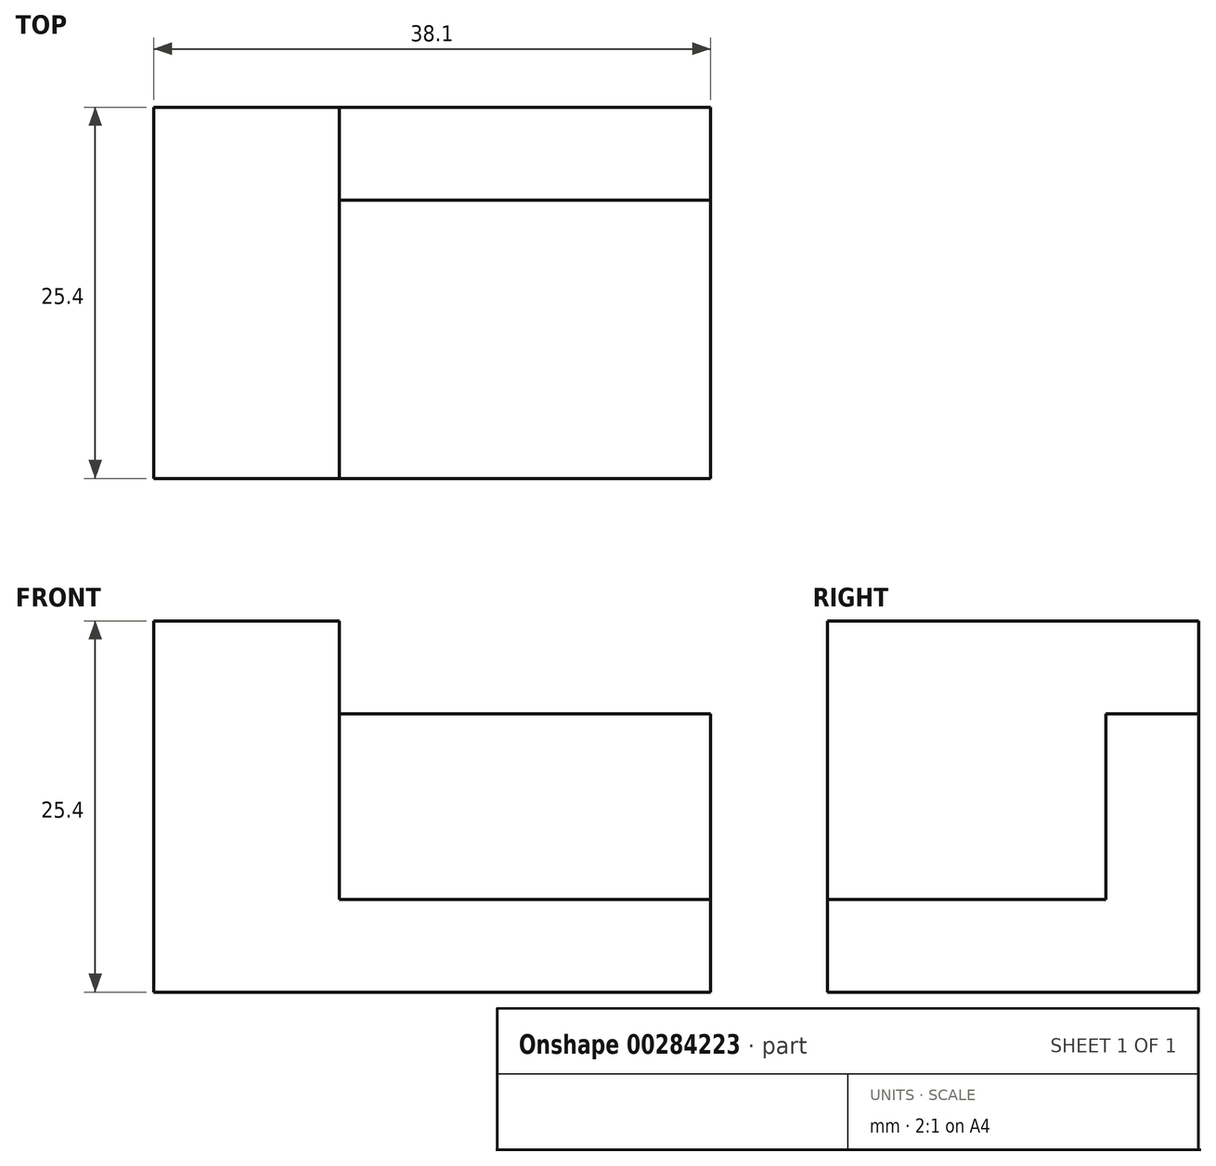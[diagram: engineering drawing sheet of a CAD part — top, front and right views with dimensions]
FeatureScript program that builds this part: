
annotation { "Feature Type Name" : "Feature", "Feature Type Description" : "" }
export const myFeature = defineFeature(function(context is Context, id is Id, definition is map)
    precondition{}
    {
        {
            var Q0;
            Q0=qCreatedBy(makeId("Front.planeOp"),FACE);
            var sketch = newSketch(context, id + "F0", { "sketchPlane" : qUnion([Q0])});
            skLineSegment(sketch, "E0", {"start": v(0, 25.4) * mm, "end": v(0, 0) * mm});
            skLineSegment(sketch, "E1", {"start": v(0, 0) * mm, "end": v(38.1, 0) * mm});
            skLineSegment(sketch, "E2", {"start": v(38.1, 0) * mm, "end": v(38.1, 6.35) * mm});
            skLineSegment(sketch, "E3", {"start": v(38.1, 6.35) * mm, "end": v(12.7, 6.35) * mm});
            skLineSegment(sketch, "E4", {"start": v(12.7, 6.35) * mm, "end": v(12.7, 25.4) * mm});
            skLineSegment(sketch, "E5", {"start": v(12.7, 25.4) * mm, "end": v(0, 25.4) * mm});
            skLineSegment(sketch, "E6", {"start": v(12.7, 19.05) * mm, "end": v(38.1, 19.05) * mm});
            skLineSegment(sketch, "E7", {"start": v(38.1, 19.05) * mm, "end": v(38.1, 6.35) * mm});
            skSolve(sketch);
        }
        {
            var Q0;
            Q0 = qSketchRegion(id + "F0", true);
            extrude(context, id + "F1", {"entities" : qUnion([Q0]), "depth" : 25.4 * mm});
        }
        {
            var Q0;
            Q0=makeQuery(id+"F1.opExtrude","SWEPT_FACE",FACE,{"disambiguationData":[OSD([sQuery(id+"F0.wireOp",EDGE,"E2"),sQuery(id+"F0.wireOp",EDGE,"E7")])]});
            var sketch = newSketch(context, id + "F2", { "sketchPlane" : qUnion([Q0])});
            skLineSegment(sketch, "E8", {"start": v(-25.4, 19.05) * mm, "end": v(-6.35, 19.05) * mm});
            skLineSegment(sketch, "E9", {"start": v(-6.35, 19.05) * mm, "end": v(-6.35, 6.35) * mm});
            skLineSegment(sketch, "E10", {"start": v(-6.35, 6.35) * mm, "end": v(-25.4, 6.35) * mm});
            skLineSegment(sketch, "E11", {"start": v(-25.4, 6.35) * mm, "end": v(-25.4, 19.05) * mm});
            skSolve(sketch);
        }
        {
            var Q0;
            Q0=makeQuery(id+"F2.imprint","IMPRINT",FACE,{"disambiguationData":[TD([[makeQuery(id+"F2.imprint","IMPRINT",EDGE,{"derivedFrom":sQuery(id+"F2.wireOp",EDGE,"E8")}),-1.0]])]});
            extrude(context, id + "F3", {"entities" : qUnion([Q0]), "operationType" : NewBodyOperationType.REMOVE, "oppositeDirection" : true, "depth" : 25.4 * mm});
        }
    });
